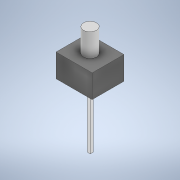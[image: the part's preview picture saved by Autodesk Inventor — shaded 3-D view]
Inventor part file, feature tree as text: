
AUTODESK INVENTOR PART (.ipt)
format: ipt  version: 2020 (Build 240168000, 168)  size: 144,896 bytes
history: native  units: mm
features: extrude x4, sketch x4, plane x4, other x3, projected_geometry x2
ambient origin geometry x8: Origin, YZ Plane, XZ Plane, XY Plane, X Axis, Y Axis, Z Axis, Center Point
bodies: Body1 (feature_tree)
feature tree (17):
  other  "Sólido1"
  extrude  "Extrusión1"  Depth=0.2mm
  extrude  "Extrusión2"  Depth=11.0mm TaperAngle=0.0deg
  other  "Eje de trabajo1"
  other  "Eje de trabajo2"
  extrude  "Extrusión3"  Depth=2.5mm
  extrude  "Extrusión4"  TaperAngle=0.0deg  [1 undecoded]
  sketch  "Boceto1"  dims[d1=0.2mm d2=0.1mm]
  sketch  "Boceto2"  dims[d3=0.1mm d4=11.0mm d5=0.0mm]
  plane  "Plano de trabajo1"
  plane  "Plano de trabajo2"
  plane  "Plano de trabajo3"
  plane  "Plano de trabajo4"
  sketch  "Boceto3"  dims[d6=2.2mm d7=2.5mm]
  projected_geometry  "Contorno proyectado1"
  sketch  "Boceto4"  dims[d8=1.6mm d9=0.0mm d10=0.0mm d11=0.9mm d12=1.1mm d13=1.25mm d14=1.6mm d15=0.0mm d16=5.0mm d17=0.0mm]
  projected_geometry  "Contorno proyectado2"
note: 1 required parameter value undecoded (feature->parameter linkage not recoverable at this tier; creation-order binding heuristic only, values carry confidence <= 0.55)
